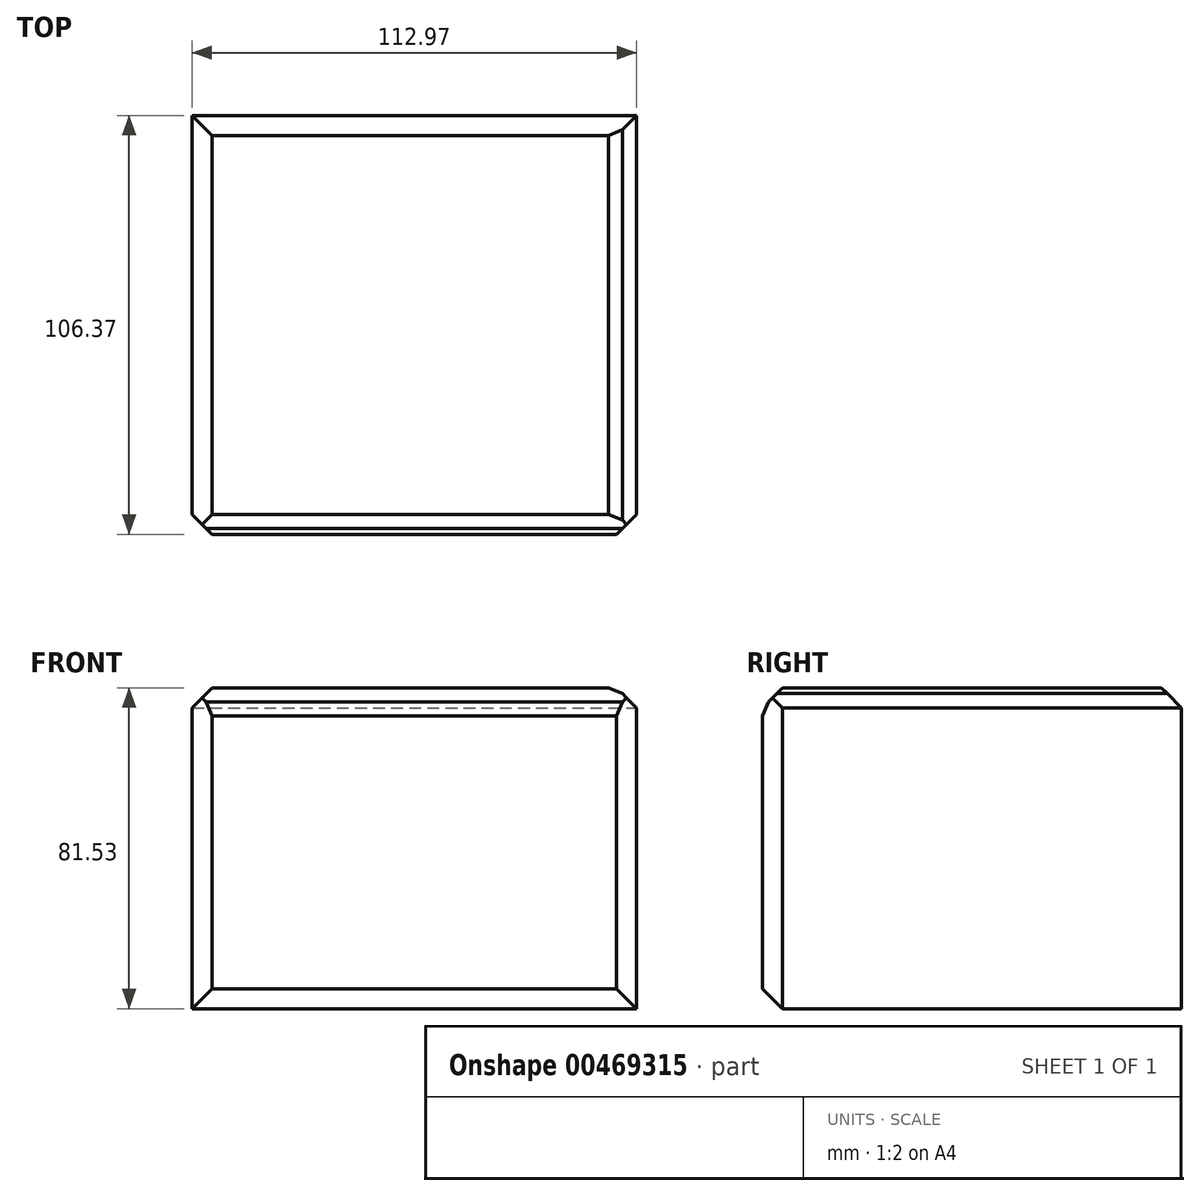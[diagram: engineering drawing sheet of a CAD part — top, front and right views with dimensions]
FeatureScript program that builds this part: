
annotation { "Feature Type Name" : "Feature", "Feature Type Description" : "" }
export const myFeature = defineFeature(function(context is Context, id is Id, definition is map)
    precondition{}
    {
        {
            var Q0;
            Q0=qCreatedBy(makeId("Top.planeOp"),FACE);
            var sketch = newSketch(context, id + "F0", { "sketchPlane" : qUnion([Q0])});
            skLineSegment(sketch, "E0.bottom", {"start": v(-75.28, 44.03) * mm, "end": v(37.69, 44.03) * mm});
            skLineSegment(sketch, "E0.top", {"start": v(-75.28, -62.34) * mm, "end": v(37.69, -62.34) * mm});
            skLineSegment(sketch, "E0.left", {"start": v(-75.28, 44.03) * mm, "end": v(-75.28, -62.34) * mm});
            skLineSegment(sketch, "E0.right", {"start": v(37.69, 44.03) * mm, "end": v(37.69, -62.34) * mm});
            skSolve(sketch);
        }
        {
            var Q0;
            Q0 = qSketchRegion(id + "F0", true);
            extrude(context, id + "F1", {"entities" : qUnion([Q0]), "depth" : 81.53 * mm});
        }
        {
            var Q0;
            Q0=makeQuery(id+"F1.opExtrude","CAP_FACE",FACE,{"disambiguationData":[OSD([sQuery(id+"F0.wireOp",EDGE,"E0.bottom"),sQuery(id+"F0.wireOp",EDGE,"E0.top"),sQuery(id+"F0.wireOp",EDGE,"E0.left"),sQuery(id+"F0.wireOp",EDGE,"E0.right")])],"isStart":false});
            chamfer(context, id + "F2", {"entities" : qUnion([Q0]), "width" : 5.08 * mm, "tangentPropagation" : true});
        }
        {
            var Q0;
            {var subQ0=sQuery(id+"F0.wireOp",EDGE,"E0.top");Q0=makeQuery(id+"Fk0ldnAIvcEYUma_1.opFillet","BLEND_EDGE",EDGE,{"blendedFrom":[makeQuery(id+"F2.opChamfer","BLEND_EDGE",EDGE,{"blendedFrom":[makeQuery(id+"F1.opExtrude","CAP_EDGE",EDGE,{"disambiguationData":[OSD([subQ0])],"isStart":false}),makeQuery(id+"F1.opExtrude","SWEPT_FACE",FACE,{"disambiguationData":[OSD([subQ0])]})],"blendedInto":[makeQuery(id+"F1.opExtrude","SWEPT_FACE",FACE,{"disambiguationData":[OSD([subQ0])]})]}),makeQuery(id+"F1.opExtrude","CAP_FACE",FACE,{"disambiguationData":[OSD([sQuery(id+"F0.wireOp",EDGE,"E0.bottom"),subQ0,sQuery(id+"F0.wireOp",EDGE,"E0.left"),sQuery(id+"F0.wireOp",EDGE,"E0.right")])],"isStart":false})],"blendedInto":[makeQuery(id+"F1.opExtrude","CAP_FACE",FACE,{"disambiguationData":[OSD([sQuery(id+"F0.wireOp",EDGE,"E0.bottom"),subQ0,sQuery(id+"F0.wireOp",EDGE,"E0.left"),sQuery(id+"F0.wireOp",EDGE,"E0.right")])],"isStart":false})]});}
            var Q1;
            {var subQ0=sQuery(id+"F0.wireOp",EDGE,"E0.left");var subQ1=sQuery(id+"F0.wireOp",EDGE,"E0.top");Q1=makeQuery(id+"Fk0ldnAIvcEYUma_1.opFillet","BLEND_EDGE",EDGE,{"blendedFrom":[makeQuery(id+"F1.opExtrude","SWEPT_EDGE",EDGE,{"disambiguationData":[OSD([subQ1,subQ0])]}),makeQuery(id+"F1.opExtrude","CAP_FACE",FACE,{"disambiguationData":[OSD([sQuery(id+"F0.wireOp",EDGE,"E0.bottom"),subQ1,subQ0,sQuery(id+"F0.wireOp",EDGE,"E0.right")])],"isStart":false})],"blendedInto":[makeQuery(id+"F1.opExtrude","CAP_FACE",FACE,{"disambiguationData":[OSD([sQuery(id+"F0.wireOp",EDGE,"E0.bottom"),subQ1,subQ0,sQuery(id+"F0.wireOp",EDGE,"E0.right")])],"isStart":false})]});}
            var Q2;
            Q2=makeQuery(id+"Fk0ldnAIvcEYUma_1.opFillet","BLEND_FACE",FACE,{"disambiguationData":[OSD([sQuery(id+"F0.wireOp",EDGE,"E0.top"),sQuery(id+"F0.wireOp",EDGE,"E0.left")])]});
            var Q3;
            {var subQ0=sQuery(id+"F0.wireOp",EDGE,"E0.right");Q3=makeQuery(id+"F2.opChamfer","BLEND_EDGE",EDGE,{"blendedFrom":[makeQuery(id+"F1.opExtrude","CAP_EDGE",EDGE,{"disambiguationData":[OSD([subQ0])],"isStart":false}),makeQuery(id+"F1.opExtrude","CAP_FACE",FACE,{"disambiguationData":[OSD([sQuery(id+"F0.wireOp",EDGE,"E0.bottom"),sQuery(id+"F0.wireOp",EDGE,"E0.top"),sQuery(id+"F0.wireOp",EDGE,"E0.left"),subQ0])],"isStart":false})],"blendedInto":[makeQuery(id+"F1.opExtrude","CAP_FACE",FACE,{"disambiguationData":[OSD([sQuery(id+"F0.wireOp",EDGE,"E0.bottom"),sQuery(id+"F0.wireOp",EDGE,"E0.top"),sQuery(id+"F0.wireOp",EDGE,"E0.left"),subQ0])],"isStart":false})]});}
            var Q4;
            {var subQ0=sQuery(id+"F0.wireOp",EDGE,"E0.right");Q4=makeQuery(id+"Fk0ldnAIvcEYUma_1.opFillet","BLEND_EDGE",EDGE,{"blendedFrom":[makeQuery(id+"F1.opExtrude","SWEPT_EDGE",EDGE,{"disambiguationData":[OSD([sQuery(id+"F0.wireOp",EDGE,"E0.top"),subQ0])]}),makeQuery(id+"F2.opChamfer","BLEND_FACE",FACE,{"disambiguationData":[OSD([subQ0])]})],"blendedInto":[makeQuery(id+"F2.opChamfer","BLEND_FACE",FACE,{"disambiguationData":[OSD([subQ0])]})]});}
            var Q5;
            Q5=makeQuery(id+"Fk0ldnAIvcEYUma_1.opFillet","BLEND_FACE",FACE,{"disambiguationData":[OSD([sQuery(id+"F0.wireOp",EDGE,"E0.top"),sQuery(id+"F0.wireOp",EDGE,"E0.right")])]});
            var Q6;
            Q6=makeQuery(id+"F1.opExtrude","SWEPT_FACE",FACE,{"disambiguationData":[OSD([sQuery(id+"F0.wireOp",EDGE,"E0.top")])]});
            var Q7;
            {var subQ0=sQuery(id+"F0.wireOp",EDGE,"E0.top");var subQ1=makeQuery(id+"F1.opExtrude","SWEPT_FACE",FACE,{"disambiguationData":[OSD([subQ0])]});Q7=makeQuery(id+"Fk0ldnAIvcEYUma_1.opFillet","BLEND_EDGE",EDGE,{"blendedFrom":[makeQuery(id+"F2.opChamfer","BLEND_EDGE",EDGE,{"blendedFrom":[makeQuery(id+"F1.opExtrude","CAP_EDGE",EDGE,{"disambiguationData":[OSD([subQ0])],"isStart":false}),subQ1],"blendedInto":[subQ1]}),subQ1],"blendedInto":[subQ1]});}
            var Q8;
            {var subQ0=sQuery(id+"F0.wireOp",EDGE,"E0.top");Q8=makeQuery(id+"Fk0ldnAIvcEYUma_1.opFillet","BLEND_FACE",FACE,{"disambiguationData":[OSD([subQ0]),TDD([makeQuery(id+"F1.opExtrude","CAP_EDGE",EDGE,{"disambiguationData":[OSD([subQ0])],"isStart":true})])]});}
            chamfer(context, id + "F3", {"entities" : qUnion([Q0, Q1, Q2, Q3, Q4, Q5, Q6, Q7, Q8]), "width" : 5.08 * mm, "tangentPropagation" : true});
        }
    });
